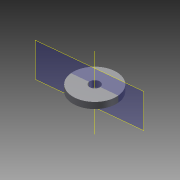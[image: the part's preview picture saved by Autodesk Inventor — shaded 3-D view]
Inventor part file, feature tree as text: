
AUTODESK INVENTOR PART (.ipt)
format: ipt  version: 2012 (Build 160160000, 160)  size: 1,998,336 bytes
history: native  units: mm
features: sketch x9, extrude x6, projected_geometry x5, other x4, plane x1
ambient origin geometry x8: Origin, YZ Plane, XZ Plane, XY Plane, X Axis, Y Axis, Z Axis, Center Point
bodies: Solid1 (feature_tree)
feature tree (25):
  other  "Gear2_LargeAndSmall.iam"
  other  "Spur Gear2:1"
  other  "Spur Gear1:1"
  sketch  "Sketch2"  dims[d0=10.0mm d1=3.3mm]
  sketch  "Sketch3"  dims[d2=10.0mm d3=0.0mm d4=0.0mm d5=0.0mm]
  other  "Work Axis1"
  extrude  "Extrusion1"  Depth=3.3mm
  sketch  "Sketch5"  dims[d10=4.0mm d11=0.0mm d12=4.0mm d13=0.0mm]
  plane  "Work Plane1"
  extrude  "Extrusion2"  TaperAngle=0.0deg  [1 undecoded]
  extrude  "Extrusion3"  Depth=10.0mm TaperAngle=0.0deg
  extrude  "Extrusion4"  Depth=4.0mm TaperAngle=0.0deg
  extrude  "Extrusion5"  [1 undecoded]
  extrude  "Extrusion6"  [1 undecoded]
  projected_geometry  "Projected Loop1"
  projected_geometry  "Projected Loop2"
  sketch  "Sketch4"  dims[d6=0.0mm d7=0.0mm d8=10.0mm d9=0.0mm]
  sketch  "Sketch6"
  projected_geometry  "Projected Loop3"
  sketch  "Sketch7"
  projected_geometry  "Projected Loop4"
  sketch  "Sketch8"
  projected_geometry  "Projected Loop6"
  sketch  "Sketch9"
  sketch  "Sketch10"
note: 3 required parameter values undecoded (feature->parameter linkage not recoverable at this tier; creation-order binding heuristic only, values carry confidence <= 0.55)
